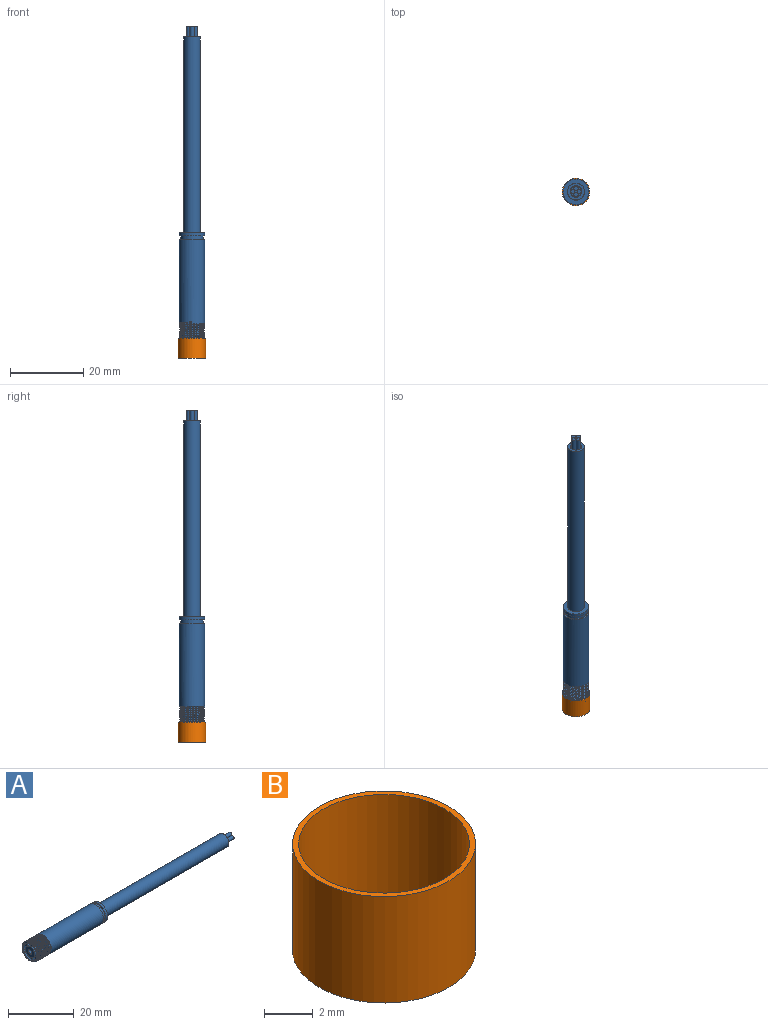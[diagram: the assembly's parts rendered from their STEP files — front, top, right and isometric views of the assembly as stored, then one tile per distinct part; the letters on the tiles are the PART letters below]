
ASSEMBLY  parts=2 mates=1
PART A: 70 faces, bbox 86.8x7.1x8.2 mm
  f0: plane 3.12x3.12mm, normal (1,0,0), area 3.5mm2, adj f61,f62,f64,f66,f68
  f1: plane 6.96x6.96mm, normal (1,0,0), area 21.4mm2, adj f58,f59
  f2: plane 6.78x6.71mm, normal (-1,0,0), area 6.6mm2, adj f5,f16,f52,f53,f54
  f3: plane 5.96x5.96mm, normal (-1,0,0), area 8.6mm2, adj f16,f17,f21,f22,f23,f24,f26,f27
  f4: cylinder r=3.48mm len=23mm, axis (-1,0,0), area 497.4mm2, adj f15,f51,f54,f56
  f5: cylinder r=3.48mm len=6.96mm, axis (-1,0,0), area 1.1mm2, adj f2,f6,f52,f54
  f6: cylinder r=3.48mm len=6.96mm, axis (-1,0,0), area 2.2mm2, adj f5,f7,f52,f54
  f7: cylinder r=3.48mm len=6.96mm, axis (-1,0,0), area 2.2mm2, adj f6,f8,f52,f54
  f8: cylinder r=3.48mm len=6.96mm, axis (-1,0,0), area 2.2mm2, adj f7,f9,f52,f54
  f9: cylinder r=3.48mm len=6.96mm, axis (-1,0,0), area 2.2mm2, adj f8,f10,f52,f54
  f10: cylinder r=3.48mm len=6.96mm, axis (-1,0,0), area 2.2mm2, adj f9,f11,f52,f54
  f11: cylinder r=3.48mm len=6.96mm, axis (-1,0,0), area 2.2mm2, adj f10,f12,f52,f54
  f12: cylinder r=3.48mm len=6.96mm, axis (-1,0,0), area 2.2mm2, adj f11,f13,f52,f54
  f13: cylinder r=3.48mm len=6.96mm, axis (-1,0,0), area 2.2mm2, adj f12,f14,f52,f54
  f14: cylinder r=3.48mm len=6.96mm, axis (-1,0,0), area 2.2mm2, adj f13,f15,f52,f54
  f15: cylinder r=3.48mm len=6.96mm, axis (-1,0,0), area 2.2mm2, adj f4,f14,f52,f54
  f16: cylinder r=2.98mm len=5.96mm, axis (-1,0,0), area 37.4mm2, adj f2,f3
  f17: cylinder r=2mm len=4mm, axis (-1,0,0), area 25.1mm2, adj f3,f18
  f18: plane 4x4mm, normal (-1,0,0), area 10.8mm2, adj f17,f19
  f19: cylinder r=0.75mm len=1.5mm, axis (-1,0,0), area 4.7mm2, adj f18,f20
  f20: plane 1.5x1.5mm, normal (-1,0,0), area 1.8mm2, adj f19
  f21: plane 1.5x0.77mm, normal (0,-1,0), area 1.2mm2, adj f3,f22,f24,f25
  f22: plane 1.5x1.46mm, normal (0,0,1), area 2.2mm2, adj f3,f21,f23,f25
  f23: plane 1.5x0.77mm, normal (0,1,0), area 1.2mm2, adj f3,f22,f24,f25
  f24: plane 1.5x1.46mm, normal (0,0,-1), area 2.2mm2, adj f3,f21,f23,f25
  f25: plane 1.46x0.77mm, normal (-1,0,0), area 1.1mm2, adj f21,f22,f23,f24
  f26: plane 1.5x0.66mm, normal (0,-0.5,0.87), area 1.2mm2, adj f3,f27,f29,f30
  f27: plane 1.5x1.26mm, normal (0,0.87,0.5), area 2.2mm2, adj f3,f26,f28,f30
  f28: plane 1.5x0.66mm, normal (0,0.5,-0.87), area 1.2mm2, adj f3,f27,f29,f30
  f29: plane 1.5x1.26mm, normal (0,-0.87,-0.5), area 2.2mm2, adj f3,f26,f28,f30
  f30: plane 1.65x1.39mm, normal (-1,0,0), area 1.1mm2, adj f26,f27,f28,f29
  f31: plane 1.5x0.66mm, normal (0,0.5,0.87), area 1.2mm2, adj f3,f32,f34,f35
  f32: plane 1.5x1.26mm, normal (0,0.87,-0.5), area 2.2mm2, adj f3,f31,f33,f35
  f33: plane 1.5x0.66mm, normal (0,-0.5,-0.87), area 1.2mm2, adj f3,f32,f34,f35
  f34: plane 1.5x1.26mm, normal (0,-0.87,0.5), area 2.2mm2, adj f3,f31,f33,f35
  f35: plane 1.65x1.39mm, normal (-1,0,0), area 1.1mm2, adj f31,f32,f33,f34
  f36: plane 1.5x0.77mm, normal (0,1,0), area 1.2mm2, adj f3,f37,f39,f40
  f37: plane 1.5x1.46mm, normal (0,0,-1), area 2.2mm2, adj f3,f36,f38,f40
  f38: plane 1.5x0.77mm, normal (0,-1,0), area 1.2mm2, adj f3,f37,f39,f40
  f39: plane 1.5x1.46mm, normal (0,0,1), area 2.2mm2, adj f3,f36,f38,f40
  f40: plane 1.46x0.77mm, normal (-1,0,0), area 1.1mm2, adj f36,f37,f38,f39
  f41: plane 1.5x0.66mm, normal (0,0.5,-0.87), area 1.2mm2, adj f3,f42,f44,f45
  f42: plane 1.5x1.26mm, normal (0,-0.87,-0.5), area 2.2mm2, adj f3,f41,f43,f45
  f43: plane 1.5x0.66mm, normal (0,-0.5,0.87), area 1.2mm2, adj f3,f42,f44,f45
  f44: plane 1.5x1.26mm, normal (0,0.87,0.5), area 2.2mm2, adj f3,f41,f43,f45
  f45: plane 1.65x1.39mm, normal (-1,0,0), area 1.1mm2, adj f41,f42,f43,f44
  f46: plane 1.5x0.66mm, normal (0,-0.5,-0.87), area 1.2mm2, adj f3,f47,f49,f50
  f47: plane 1.5x1.26mm, normal (0,-0.87,0.5), area 2.2mm2, adj f3,f46,f48,f50
  f48: plane 1.5x0.66mm, normal (0,0.5,0.87), area 1.2mm2, adj f3,f47,f49,f50
  f49: plane 1.5x1.26mm, normal (0,0.87,-0.5), area 2.2mm2, adj f3,f46,f48,f50
  f50: plane 1.65x1.39mm, normal (-1,0,0), area 1.1mm2, adj f46,f47,f48,f49
  f51: plane 0.4x0.3mm, normal (0,0,1), area 0.1mm2, adj f4,f52,f53,f54
  f52: bspline ~8.04x6.96mm, area 72.4mm2, adj f2,f5,f6,f7,f8,f9,f10,f11
  f53: cylinder r=3.18mm len=6.36mm, axis (1,0,0), area 41.6mm2, adj f2,f51,f52,f54
  f54: bspline ~8.04x6.96mm, area 76mm2, adj f2,f4,f5,f6,f7,f8,f9,f10
  f55: plane 6.96x6.96mm, normal (-1,0,0), area 7.9mm2, adj f57,f58
  f56: plane 6.96x6.96mm, normal (1,0,0), area 7.9mm2, adj f4,f57
  f57: cylinder r=3.1mm len=6.2mm, axis (-1,0,0), area 19.5mm2, adj f55,f56
  f58: cylinder r=3.48mm len=6.96mm, axis (-1,0,0), area 17.5mm2, adj f1,f55
  f59: cylinder r=2.3mm len=53.5mm, axis (-1,0,0), area 773.1mm2, adj f1,f60
  f60: plane 4.6x4.6mm, normal (1,0,0), area 9mm2, adj f59,f61
  f61: cylinder r=1.56mm len=5mm, axis (1,0,0), area 49.1mm2, adj f0,f60
  f62: cylinder r=0.58mm len=8mm, axis (-1,0,0), area 29.1mm2, adj f0,f63
  f63: plane 1.16x1.16mm, normal (1,0,0), area 1.1mm2, adj f62
  f64: cylinder r=0.58mm len=8mm, axis (-1,0,0), area 29.1mm2, adj f0,f65
  f65: plane 1.16x1.16mm, normal (1,0,0), area 1.1mm2, adj f64
  f66: cylinder r=0.58mm len=8mm, axis (-1,0,0), area 29.1mm2, adj f0,f67
  f67: plane 1.16x1.16mm, normal (1,0,0), area 1.1mm2, adj f66
  f68: cylinder r=0.58mm len=8mm, axis (-1,0,0), area 29.1mm2, adj f0,f69
  f69: plane 1.16x1.16mm, normal (1,0,0), area 1.1mm2, adj f68
PART B: 4 faces, bbox 7.5x7.5x5.3 mm
  f0: cylinder r=3.75mm len=7.5mm, axis (0,0,-1), area 125.8mm2, adj f1,f2
  f1: plane 7.5x7.5mm, normal (0,0,1), area 5.7mm2, adj f0,f3
  f2: plane 7.5x7.5mm, normal (0,0,-1), area 5.7mm2, adj f0,f3
  f3: cylinder r=3.5mm len=7mm, axis (0,0,1), area 117.4mm2, adj f1,f2
PLACE A rot(axis=(0,-1,0),90deg) t=(74.68,52.96,-70.29)mm fixed
PLACE B t=(74.68,52.96,-74.44)mm
MATE slider B.f0 <-> A.f4  axis (0,0,-1) through (74.68,52.96,-74.44)mm
